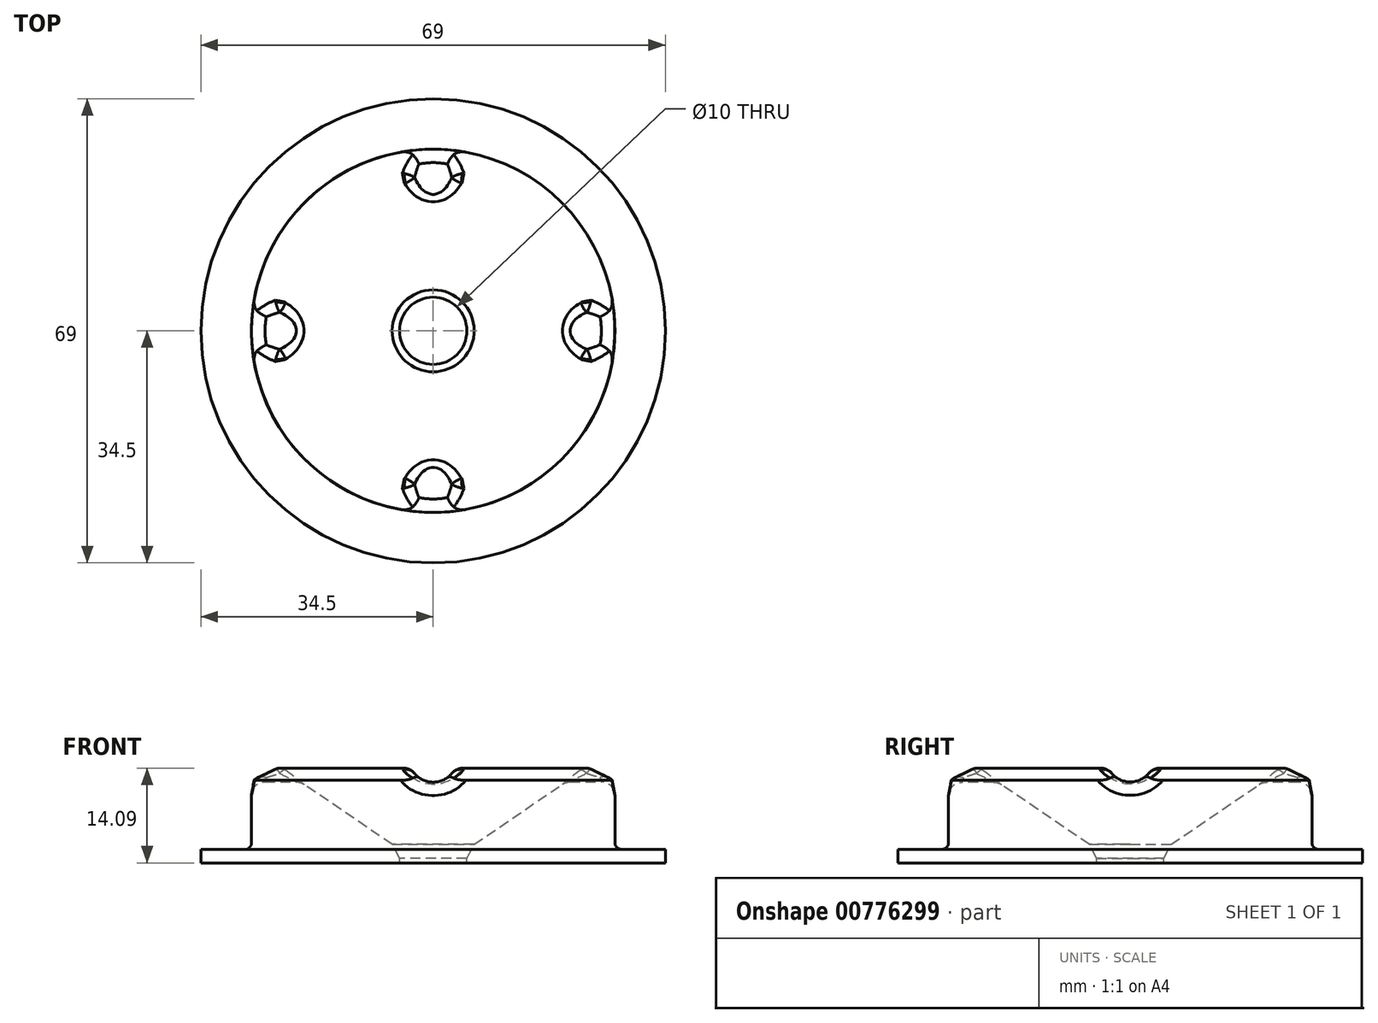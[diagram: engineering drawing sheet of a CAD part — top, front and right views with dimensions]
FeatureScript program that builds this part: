
annotation { "Feature Type Name" : "Feature", "Feature Type Description" : "" }
export const myFeature = defineFeature(function(context is Context, id is Id, definition is map)
    precondition{}
    {
        {
            var Q0;
            Q0=qCreatedBy(makeId("Front.planeOp"),FACE);
            var sketch = newSketch(context, id + "F0", { "sketchPlane" : qUnion([Q0])});
            skLineSegment(sketch, "E0.bottom", {"start": v(0, 0) * mm, "end": v(34.5, 0) * mm});
            skLineSegment(sketch, "E0.top", {"start": v(27, 2) * mm, "end": v(34.5, 2) * mm});
            skLineSegment(sketch, "E0.left", {"start": v(0, 0) * mm, "end": v(0, 2) * mm});
            skLineSegment(sketch, "E0.right", {"start": v(34.5, 0) * mm, "end": v(34.5, 2) * mm});
            skLineSegment(sketch, "E1", {"start": v(34.5, 2) * mm, "end": v(27, 2) * mm, "construction": true});
            skLineSegment(sketch, "E2", {"start": v(27, 2) * mm, "end": v(27, 17) * mm});
            skLineSegment(sketch, "E3", {"start": v(0, 2) * mm, "end": v(3.62, 2) * mm, "construction": true});
            skLineSegment(sketch, "E4", {"start": v(0, 2) * mm, "end": v(5, 2) * mm, "construction": true});
            skLineSegment(sketch, "E5", {"start": v(27, 17) * mm, "end": v(5, 2) * mm});
            skLineSegment(sketch, "E6", {"start": v(5, 2) * mm, "end": v(0, 2) * mm});
            skSolve(sketch);
        }
        {
            var Q0;
            Q0=makeQuery(id+"F0.imprint","IMPRINT",FACE,{"disambiguationData":[TD([[makeQuery(id+"F0.imprint","IMPRINT",EDGE,{"derivedFrom":sQuery(id+"F0.wireOp",EDGE,"E0.bottom")}),1.0]])]});
            var Q1;
            Q1=sQuery(id+"F0.wireOp",EDGE,"E0.left");
            revolve(context, id + "F1", {"surfaceOperationType" : NewSurfaceOperationType.NEW, "entities" : qUnion([Q0]), "axis" : qUnion([Q1]), "revolveType" : RevolveType.FULL});
        }
        {
            var Q0;
            Q0=makeQuery(id+"F1.opRevolve","SWEPT_FACE",FACE,{"disambiguationData":[OSD([sQuery(id+"F0.wireOp",EDGE,"E6")])]});
            var sketch = newSketch(context, id + "F2", { "sketchPlane" : qUnion([Q0])});
            skCircle(sketch, "E7", {"center": v(0, 0) * mm, "radius": 5 * mm});
            skSolve(sketch);
        }
        {
            var Q0;
            Q0=makeQuery(id+"F2.imprint","IMPRINT",FACE,{"disambiguationData":[TD([[makeQuery(id+"F2.imprint","IMPRINT",EDGE,{"derivedFrom":sQuery(id+"F2.wireOp",EDGE,"E7")}),-1.0]])]});
            extrude(context, id + "F3", {"entities" : qUnion([Q0]), "operationType" : NewBodyOperationType.REMOVE, "oppositeDirection" : true, "depth" : 25 * mm, "offsetDistance" : 25 * mm});
        }
        {
            var Q0;
            Q0=makeQuery(id+"F1.opRevolve","SWEPT_EDGE",EDGE,{"disambiguationData":[OSD([sQuery(id+"F0.wireOp",EDGE,"E2"),sQuery(id+"F0.wireOp",EDGE,"E5")])]});
            var Q1;
            Q1=makeQuery(id+"F3.boolean.opBoolean","MERGE",EDGE,{"derivedFrom":[makeQuery(id+"F1.opRevolve","SWEPT_EDGE",EDGE,{"disambiguationData":[OSD([sQuery(id+"F0.wireOp",EDGE,"E5"),sQuery(id+"F0.wireOp",EDGE,"E6")])]}),makeQuery(id+"F3.opExtrude","CAP_EDGE",EDGE,{"disambiguationData":[OSD([sQuery(id+"F2.wireOp",EDGE,"E7")])],"isStart":true})]});
            chamfer(context, id + "F4", {"entities" : qUnion([Q0, Q1]), "width" : 2.5 * mm, "tangentPropagation" : true});
        }
        {
            var Q0;
            Q0=makeQuery(id+"F1.opRevolve","SWEPT_EDGE",EDGE,{"disambiguationData":[OSD([sQuery(id+"F0.wireOp",EDGE,"E0.top"),sQuery(id+"F0.wireOp",EDGE,"E2")])]});
            fillet(context, id + "F5", {"entities" : qUnion([Q0]), "radius" : 1 * mm, "tangentPropagation" : true, "allowEdgeOverflow" : false});
        }
        {
            var Q0;
            Q0=qCreatedBy(makeId("Front.planeOp"),FACE);
            var sketch = newSketch(context, id + "F6", { "sketchPlane" : qUnion([Q0])});
            skCircle(sketch, "E8", {"center": v(0, 15.6) * mm, "radius": 3.6 * mm});
            skSolve(sketch);
        }
        {
            var Q0;
            Q0=makeQuery(id+"F6.imprint","IMPRINT",FACE,{"disambiguationData":[TD([[makeQuery(id+"F6.imprint","IMPRINT",EDGE,{"derivedFrom":sQuery(id+"F6.wireOp",EDGE,"E8")}),1.0]])]});
            extrude(context, id + "F7", {"entities" : qUnion([Q0]), "operationType" : NewBodyOperationType.REMOVE, "endBound" : BoundingType.SYMMETRIC, "oppositeDirection" : true, "depth" : 70 * mm, "offsetDistance" : 25 * mm});
        }
        {
            var Q0;
            Q0=qCreatedBy(makeId("Right.planeOp"),FACE);
            var sketch = newSketch(context, id + "F8", { "sketchPlane" : qUnion([Q0])});
            skCircle(sketch, "E9", {"center": v(0, 15.64) * mm, "radius": 3.6 * mm});
            skSolve(sketch);
        }
        {
            var Q0;
            Q0=makeQuery(id+"F8.imprint","IMPRINT",FACE,{"disambiguationData":[TD([[makeQuery(id+"F8.imprint","IMPRINT",EDGE,{"derivedFrom":sQuery(id+"F8.wireOp",EDGE,"E9")}),1.0]])]});
            extrude(context, id + "F9", {"entities" : qUnion([Q0]), "operationType" : NewBodyOperationType.REMOVE, "endBound" : BoundingType.SYMMETRIC, "oppositeDirection" : true, "depth" : 70 * mm, "offsetDistance" : 25 * mm});
        }
        {
            var Q0;
            Q0=makeQuery(id+"F7.boolean.opBoolean","COPY",FACE,{"disambiguationData":[OD(1.0)],"derivedFrom":makeQuery(id+"F7.opExtrude","SWEPT_FACE",FACE,{"disambiguationData":[OSD([sQuery(id+"F6.wireOp",EDGE,"E8")])]})});
            var Q1;
            Q1=makeQuery(id+"F9.boolean.opBoolean","COPY",FACE,{"disambiguationData":[OD(1.0)],"derivedFrom":makeQuery(id+"F9.opExtrude","SWEPT_FACE",FACE,{"disambiguationData":[OSD([sQuery(id+"F8.wireOp",EDGE,"E9")])]})});
            var Q2;
            Q2=makeQuery(id+"F7.boolean.opBoolean","COPY",FACE,{"disambiguationData":[OD(0.0)],"derivedFrom":makeQuery(id+"F7.opExtrude","SWEPT_FACE",FACE,{"disambiguationData":[OSD([sQuery(id+"F6.wireOp",EDGE,"E8")])]})});
            var Q3;
            Q3=makeQuery(id+"F9.boolean.opBoolean","COPY",FACE,{"disambiguationData":[OD(0.0)],"derivedFrom":makeQuery(id+"F9.opExtrude","SWEPT_FACE",FACE,{"disambiguationData":[OSD([sQuery(id+"F8.wireOp",EDGE,"E9")])]})});
            fillet(context, id + "F10", {"entities" : qUnion([Q0, Q1, Q2, Q3]), "radius" : 2 * mm, "tangentPropagation" : true, "allowEdgeOverflow" : false});
        }
        {
            var Q0;
            {var subQ0=sQuery(id+"F0.wireOp",EDGE,"E5");var subQ1=makeQuery(id+"F1.opRevolve","SWEPT_FACE",FACE,{"disambiguationData":[OSD([subQ0])]});var subQ2=sQuery(id+"F0.wireOp",EDGE,"E2");Q0=makeQuery(id+"F9.boolean.opBoolean","SPLIT",EDGE,{"disambiguationData":[TD([makeQuery(id+"F7.boolean.opBoolean","COPY",FACE,{"disambiguationData":[OD(1.0)],"derivedFrom":makeQuery(id+"F7.opExtrude","SWEPT_FACE",FACE,{"disambiguationData":[OSD([sQuery(id+"F6.wireOp",EDGE,"E8")])]})})])],"derivedFrom":makeQuery(id+"F7.boolean.opBoolean","SPLIT",EDGE,{"disambiguationData":[OD(0.0)],"derivedFrom":makeQuery(id+"F4.opChamfer","BLEND_EDGE",EDGE,{"blendedFrom":[makeQuery(id+"F1.opRevolve","SWEPT_EDGE",EDGE,{"disambiguationData":[OSD([subQ2,subQ0])]}),subQ1],"blendedInto":[subQ1]})})});}
            var Q1;
            {var subQ0=sQuery(id+"F0.wireOp",EDGE,"E5");var subQ1=makeQuery(id+"F1.opRevolve","SWEPT_FACE",FACE,{"disambiguationData":[OSD([subQ0])]});var subQ2=sQuery(id+"F0.wireOp",EDGE,"E2");Q1=makeQuery(id+"F9.boolean.opBoolean","SPLIT",EDGE,{"disambiguationData":[TD([makeQuery(id+"F7.boolean.opBoolean","COPY",FACE,{"disambiguationData":[OD(1.0)],"derivedFrom":makeQuery(id+"F7.opExtrude","SWEPT_FACE",FACE,{"disambiguationData":[OSD([sQuery(id+"F6.wireOp",EDGE,"E8")])]})})])],"derivedFrom":makeQuery(id+"F7.boolean.opBoolean","SPLIT",EDGE,{"disambiguationData":[OD(1.0)],"derivedFrom":makeQuery(id+"F4.opChamfer","BLEND_EDGE",EDGE,{"blendedFrom":[makeQuery(id+"F1.opRevolve","SWEPT_EDGE",EDGE,{"disambiguationData":[OSD([subQ2,subQ0])]}),subQ1],"blendedInto":[subQ1]})})});}
            var Q2;
            {var subQ0=sQuery(id+"F0.wireOp",EDGE,"E5");var subQ1=makeQuery(id+"F1.opRevolve","SWEPT_FACE",FACE,{"disambiguationData":[OSD([subQ0])]});var subQ2=sQuery(id+"F0.wireOp",EDGE,"E2");Q2=makeQuery(id+"F9.boolean.opBoolean","SPLIT",EDGE,{"disambiguationData":[TD([makeQuery(id+"F7.boolean.opBoolean","COPY",FACE,{"disambiguationData":[OD(0.0)],"derivedFrom":makeQuery(id+"F7.opExtrude","SWEPT_FACE",FACE,{"disambiguationData":[OSD([sQuery(id+"F6.wireOp",EDGE,"E8")])]})})])],"derivedFrom":makeQuery(id+"F7.boolean.opBoolean","SPLIT",EDGE,{"disambiguationData":[OD(0.0)],"derivedFrom":makeQuery(id+"F4.opChamfer","BLEND_EDGE",EDGE,{"blendedFrom":[makeQuery(id+"F1.opRevolve","SWEPT_EDGE",EDGE,{"disambiguationData":[OSD([subQ2,subQ0])]}),subQ1],"blendedInto":[subQ1]})})});}
            var Q3;
            {var subQ0=sQuery(id+"F0.wireOp",EDGE,"E5");var subQ1=makeQuery(id+"F1.opRevolve","SWEPT_FACE",FACE,{"disambiguationData":[OSD([subQ0])]});var subQ2=sQuery(id+"F0.wireOp",EDGE,"E2");Q3=makeQuery(id+"F9.boolean.opBoolean","SPLIT",EDGE,{"disambiguationData":[TD([makeQuery(id+"F7.boolean.opBoolean","COPY",FACE,{"disambiguationData":[OD(0.0)],"derivedFrom":makeQuery(id+"F7.opExtrude","SWEPT_FACE",FACE,{"disambiguationData":[OSD([sQuery(id+"F6.wireOp",EDGE,"E8")])]})})])],"derivedFrom":makeQuery(id+"F7.boolean.opBoolean","SPLIT",EDGE,{"disambiguationData":[OD(1.0)],"derivedFrom":makeQuery(id+"F4.opChamfer","BLEND_EDGE",EDGE,{"blendedFrom":[makeQuery(id+"F1.opRevolve","SWEPT_EDGE",EDGE,{"disambiguationData":[OSD([subQ2,subQ0])]}),subQ1],"blendedInto":[subQ1]})})});}
            fillet(context, id + "F11", {"entities" : qUnion([Q0, Q1, Q2, Q3]), "radius" : 1.5 * mm, "tangentPropagation" : true, "allowEdgeOverflow" : false});
        }
    });
